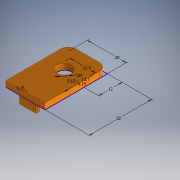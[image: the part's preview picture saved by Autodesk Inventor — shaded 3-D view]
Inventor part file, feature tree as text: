
AUTODESK INVENTOR PART (.ipt)
format: ipt  version: 2018 (Build 220112000, 112)  size: 137,728 bytes
history: native  units: mm
features: extrude x3, fillet x2, sketch x1
ambient origin geometry x8: Origin, YZ Plane, XZ Plane, XY Plane, X Axis, Y Axis, Z Axis, Center Point
bodies: Solid1 (feature_tree)
feature tree (6):
  sketch  "Sketch1"  dims[d0=20.0mm d1=32.0mm d2=0.15mm d3=0.15mm d5=7.07mm d6=12.9mm d7=13.7mm d8=12.0mm d9=3.0mm d10=0.0mm d11=3.0mm d12=0.0mm d13=4.0mm d14=0.15mm d15=5.0mm d16=0.0mm d17=0.5mm]
  extrude  "Extrusion1"  Depth=0.5mm
  extrude  "Extrusion2"  Depth=0.5mm
  fillet  "Fillet1"  Radius=12.0mm
  extrude  "Extrusion3"  Depth=3.0mm TaperAngle=0.0deg
  fillet  "Fillet2"  Radius=3.0mm
